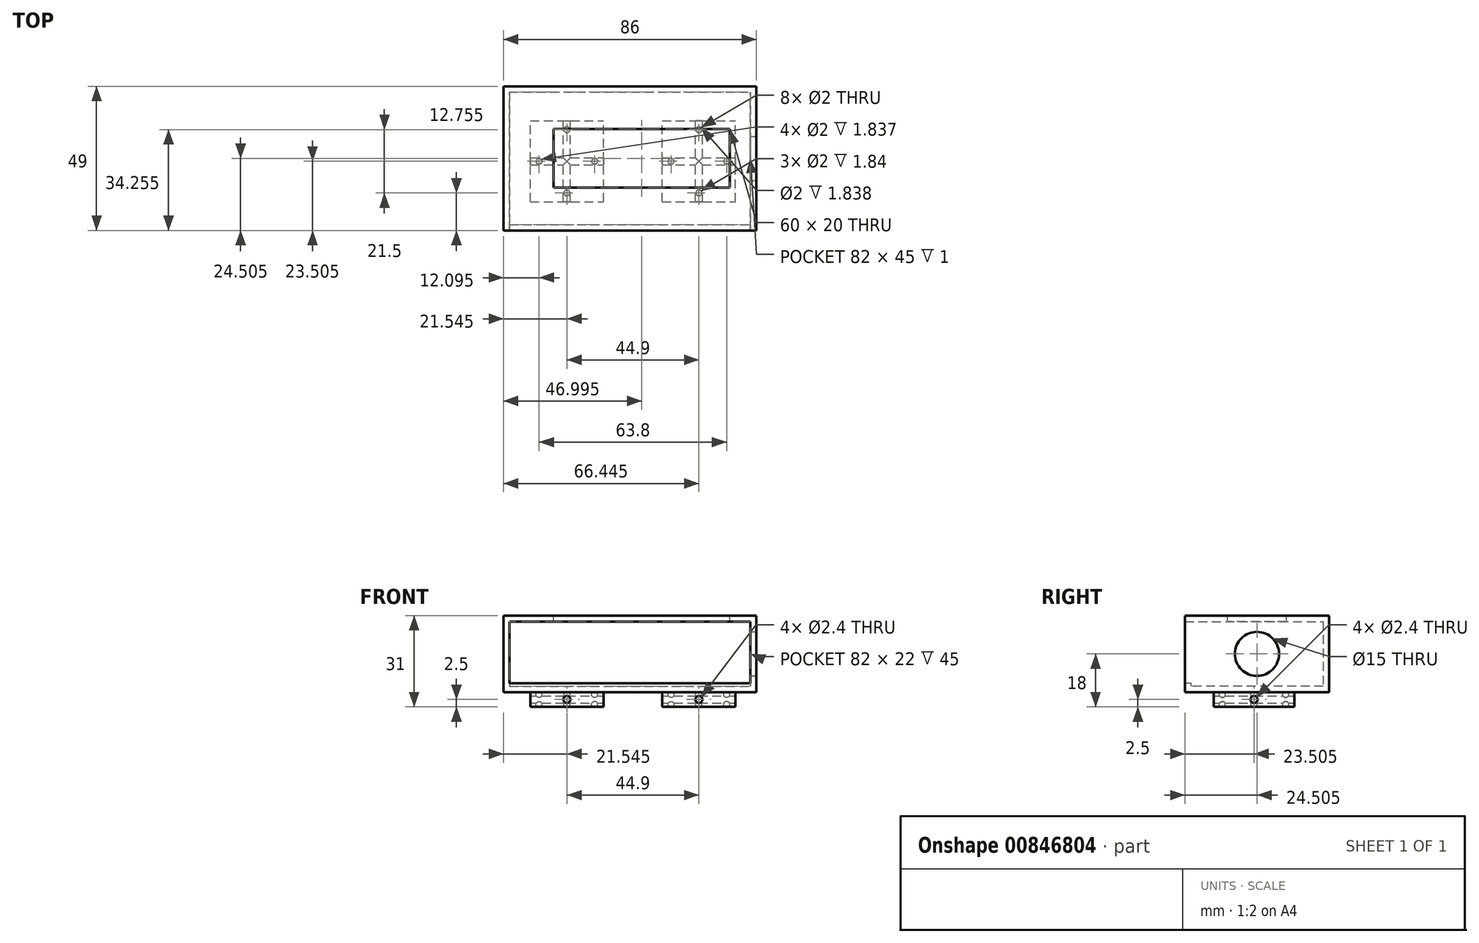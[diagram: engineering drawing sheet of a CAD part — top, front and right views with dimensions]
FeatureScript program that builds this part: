
annotation { "Feature Type Name" : "Feature", "Feature Type Description" : "" }
export const myFeature = defineFeature(function(context is Context, id is Id, definition is map)
    precondition{}
    {
        {
            var Q0;
            Q0=qCreatedBy(makeId("Top.planeOp"),FACE);
            var sketch = newSketch(context, id + "F0", { "sketchPlane" : qUnion([Q0])});
            skLineSegment(sketch, "E0.bottom", {"start": v(-27.92, 18.33) * mm, "end": v(54.08, 18.33) * mm});
            skLineSegment(sketch, "E0.top", {"start": v(-27.92, -26.67) * mm, "end": v(54.08, -26.67) * mm});
            skLineSegment(sketch, "E0.left", {"start": v(-27.92, 18.33) * mm, "end": v(-27.92, -26.67) * mm});
            skLineSegment(sketch, "E0.right", {"start": v(54.08, 18.33) * mm, "end": v(54.08, -26.67) * mm});
            skLineSegment(sketch, "E1.bottom", {"start": v(-29.92, 20.33) * mm, "end": v(56.08, 20.33) * mm});
            skLineSegment(sketch, "E1.top", {"start": v(-29.92, -28.67) * mm, "end": v(56.08, -28.67) * mm});
            skLineSegment(sketch, "E1.left", {"start": v(-29.92, 20.33) * mm, "end": v(-29.92, -28.67) * mm});
            skLineSegment(sketch, "E1.right", {"start": v(56.08, 20.33) * mm, "end": v(56.08, -28.67) * mm});
            skSolve(sketch);
        }
        {
            var Q0;
            Q0=makeQuery(id+"F0.imprint","IMPRINT",FACE,{"disambiguationData":[TD([[makeQuery(id+"F0.imprint","IMPRINT",EDGE,{"derivedFrom":sQuery(id+"F0.wireOp",EDGE,"E0.bottom")}),-1.0]])]});
            extrude(context, id + "F1", {"entities" : qUnion([Q0]), "depth" : 2 * mm, "offsetDistance" : 25 * mm});
        }
        {
            var Q0;
            Q0=makeQuery(id+"F0.imprint","IMPRINT",FACE,{"disambiguationData":[TD([[makeQuery(id+"F0.imprint","IMPRINT",EDGE,{"derivedFrom":sQuery(id+"F0.wireOp",EDGE,"E0.bottom")}),1.0]])]});
            extrude(context, id + "F2", {"entities" : qUnion([Q0]), "operationType" : NewBodyOperationType.ADD, "depth" : 26 * mm, "offsetDistance" : 25 * mm});
        }
        {
            var Q0;
            Q0=makeQuery(id+"F2.opExtrude","SWEPT_FACE",FACE,{"disambiguationData":[OSD([sQuery(id+"F0.wireOp",EDGE,"E0.bottom")])]});
            var sketch = newSketch(context, id + "F3", { "sketchPlane" : qUnion([Q0])});
            skLineSegment(sketch, "E2.bottom", {"start": v(-27.92, 26) * mm, "end": v(54.08, 26) * mm});
            skLineSegment(sketch, "E2.top", {"start": v(-27.92, 24) * mm, "end": v(54.08, 24) * mm});
            skLineSegment(sketch, "E2.left", {"start": v(-27.92, 26) * mm, "end": v(-27.92, 24) * mm});
            skLineSegment(sketch, "E2.right", {"start": v(54.08, 26) * mm, "end": v(54.08, 24) * mm});
            skSolve(sketch);
        }
        {
            var Q0;
            Q0=makeQuery(id+"F3.imprint","IMPRINT",FACE,{"disambiguationData":[TD([[makeQuery(id+"F3.imprint","IMPRINT",EDGE,{"derivedFrom":sQuery(id+"F3.wireOp",EDGE,"E2.bottom")}),-1.0]])]});
            extrude(context, id + "F4", {"entities" : qUnion([Q0]), "operationType" : NewBodyOperationType.ADD, "endBound" : BoundingType.UP_TO_NEXT, "depth" : 25 * mm, "offsetDistance" : 25 * mm});
        }
        {
            var Q0;
            Q0=makeQuery(id+"F2.opExtrude","SWEPT_FACE",FACE,{"disambiguationData":[OSD([sQuery(id+"F0.wireOp",EDGE,"E1.top")])]});
            var sketch = newSketch(context, id + "F5", { "sketchPlane" : qUnion([Q0])});
            skLineSegment(sketch, "E3.bottom", {"start": v(-27.92, 24) * mm, "end": v(54.08, 24) * mm});
            skLineSegment(sketch, "E3.top", {"start": v(-27.92, 3) * mm, "end": v(54.08, 3) * mm});
            skLineSegment(sketch, "E3.left", {"start": v(-27.92, 24) * mm, "end": v(-27.92, 3) * mm});
            skLineSegment(sketch, "E3.right", {"start": v(54.08, 24) * mm, "end": v(54.08, 3) * mm});
            skSolve(sketch);
        }
        {
            var Q0;
            Q0=makeQuery(id+"F5.imprint","IMPRINT",FACE,{"disambiguationData":[TD([[makeQuery(id+"F5.imprint","IMPRINT",EDGE,{"derivedFrom":sQuery(id+"F5.wireOp",EDGE,"E3.bottom")}),-1.0]])]});
            extrude(context, id + "F6", {"entities" : qUnion([Q0]), "operationType" : NewBodyOperationType.REMOVE, "oppositeDirection" : true, "depth" : 2 * mm, "offsetDistance" : 25 * mm});
        }
        {
            var Q0;
            Q0=makeQuery(id+"F4.boolean.opBoolean","MERGE",FACE,{"derivedFrom":[makeQuery(id+"F2.opExtrude","CAP_FACE",FACE,{"disambiguationData":[OSD([sQuery(id+"F0.wireOp",EDGE,"E0.bottom"),sQuery(id+"F0.wireOp",EDGE,"E0.top"),sQuery(id+"F0.wireOp",EDGE,"E0.left"),sQuery(id+"F0.wireOp",EDGE,"E0.right"),sQuery(id+"F0.wireOp",EDGE,"E1.bottom"),sQuery(id+"F0.wireOp",EDGE,"E1.top"),sQuery(id+"F0.wireOp",EDGE,"E1.left"),sQuery(id+"F0.wireOp",EDGE,"E1.right")])],"isStart":false}),makeQuery(id+"F4.opExtrude","SWEPT_FACE",FACE,{"disambiguationData":[OSD([sQuery(id+"F3.wireOp",EDGE,"E2.bottom")])]})]});
            var sketch = newSketch(context, id + "F7", { "sketchPlane" : qUnion([Q0])});
            skLineSegment(sketch, "E4.bottom", {"start": v(-12.92, -14.17) * mm, "end": v(47.08, -14.17) * mm});
            skLineSegment(sketch, "E4.top", {"start": v(-12.92, 5.83) * mm, "end": v(47.08, 5.83) * mm});
            skLineSegment(sketch, "E4.left", {"start": v(-12.92, -14.17) * mm, "end": v(-12.92, 5.83) * mm});
            skLineSegment(sketch, "E4.right", {"start": v(47.08, -14.17) * mm, "end": v(47.08, 5.83) * mm});
            skSolve(sketch);
        }
        {
            var Q0;
            Q0=makeQuery(id+"F7.imprint","IMPRINT",FACE,{"disambiguationData":[TD([[makeQuery(id+"F7.imprint","IMPRINT",EDGE,{"derivedFrom":sQuery(id+"F7.wireOp",EDGE,"E4.bottom")}),1.0]])]});
            extrude(context, id + "F8", {"entities" : qUnion([Q0]), "operationType" : NewBodyOperationType.REMOVE, "endBound" : BoundingType.UP_TO_NEXT, "oppositeDirection" : true, "depth" : 25 * mm, "offsetDistance" : 25 * mm});
        }
        {
            var Q0;
            Q0=makeQuery(id+"F2.opExtrude","SWEPT_FACE",FACE,{"disambiguationData":[OSD([sQuery(id+"F0.wireOp",EDGE,"E1.right")])]});
            var sketch = newSketch(context, id + "F9", { "sketchPlane" : qUnion([Q0])});
            skCircle(sketch, "E5", {"center": v(-4.17, 13) * mm, "radius": 7.5 * mm});
            skPoint(sketch, "E5.centerSnap0", {"position": v(-4.17, 26) * mm});
            skPoint(sketch, "E5.centerSnap1", {"position": v(20.33, 13) * mm});
            skSolve(sketch);
        }
        {
            var Q0;
            Q0=makeQuery(id+"F9.imprint","IMPRINT",FACE,{"disambiguationData":[TD([[makeQuery(id+"F9.imprint","IMPRINT",EDGE,{"derivedFrom":sQuery(id+"F9.wireOp",EDGE,"E5")}),1.0]])]});
            extrude(context, id + "F10", {"entities" : qUnion([Q0]), "operationType" : NewBodyOperationType.REMOVE, "endBound" : BoundingType.UP_TO_NEXT, "oppositeDirection" : true, "depth" : 25 * mm, "offsetDistance" : 25 * mm});
        }
        {
            var Q0;
            {var subQ0=sQuery(id+"F0.wireOp",EDGE,"E0.right");var subQ1=sQuery(id+"F0.wireOp",EDGE,"E0.left");var subQ2=sQuery(id+"F0.wireOp",EDGE,"E0.top");var subQ3=sQuery(id+"F0.wireOp",EDGE,"E0.bottom");Q0=makeQuery(id+"F2.boolean.opBoolean","MERGE",FACE,{"derivedFrom":[makeQuery(id+"F1.opExtrude","CAP_FACE",FACE,{"disambiguationData":[OSD([subQ3,subQ2,subQ1,subQ0])],"isStart":true}),makeQuery(id+"F2.opExtrude","CAP_FACE",FACE,{"disambiguationData":[OSD([subQ3,subQ2,subQ1,subQ0,sQuery(id+"F0.wireOp",EDGE,"E1.bottom"),sQuery(id+"F0.wireOp",EDGE,"E1.top"),sQuery(id+"F0.wireOp",EDGE,"E1.left"),sQuery(id+"F0.wireOp",EDGE,"E1.right")])],"isStart":true})]});}
            var sketch = newSketch(context, id + "F11", { "sketchPlane" : qUnion([Q0])});
            skLineSegment(sketch, "E6.bottom", {"start": v(-17.82, 15.92) * mm, "end": v(1.08, 15.92) * mm});
            skLineSegment(sketch, "E6.top", {"start": v(-17.82, -5.58) * mm, "end": v(1.08, -5.58) * mm});
            skLineSegment(sketch, "E6.left", {"start": v(-17.82, 15.92) * mm, "end": v(-17.82, -5.58) * mm});
            skLineSegment(sketch, "E6.right", {"start": v(1.08, 15.92) * mm, "end": v(1.08, -5.58) * mm});
            skLineSegment(sketch, "E7.bottom", {"start": v(-20.82, 18.92) * mm, "end": v(4.08, 18.92) * mm});
            skLineSegment(sketch, "E7.top", {"start": v(-20.82, -8.58) * mm, "end": v(4.08, -8.58) * mm});
            skLineSegment(sketch, "E7.left", {"start": v(-20.82, 18.92) * mm, "end": v(-20.82, -8.58) * mm});
            skLineSegment(sketch, "E7.right", {"start": v(4.08, 18.92) * mm, "end": v(4.08, -8.58) * mm});
            skCircle(sketch, "E8", {"center": v(1.08, 5.17) * mm, "radius": 1 * mm});
            skCircle(sketch, "E9", {"center": v(-8.37, -5.58) * mm, "radius": 1 * mm});
            skCircle(sketch, "E10", {"center": v(-17.82, 5.17) * mm, "radius": 1 * mm});
            skCircle(sketch, "E11", {"center": v(-8.37, 15.92) * mm, "radius": 1 * mm});
            skLineSegment(sketch, "E12.bottom", {"start": v(24.08, 18.92) * mm, "end": v(48.98, 18.92) * mm});
            skLineSegment(sketch, "E12.top", {"start": v(24.08, -8.58) * mm, "end": v(48.98, -8.58) * mm});
            skLineSegment(sketch, "E12.left", {"start": v(24.08, 18.92) * mm, "end": v(24.08, -8.58) * mm});
            skLineSegment(sketch, "E12.right", {"start": v(48.98, 18.92) * mm, "end": v(48.98, -8.58) * mm});
            skLineSegment(sketch, "E13.bottom", {"start": v(27.08, 15.92) * mm, "end": v(45.98, 15.92) * mm});
            skLineSegment(sketch, "E13.top", {"start": v(27.08, -5.58) * mm, "end": v(45.98, -5.58) * mm});
            skLineSegment(sketch, "E13.left", {"start": v(27.08, 15.92) * mm, "end": v(27.08, -5.58) * mm});
            skLineSegment(sketch, "E13.right", {"start": v(45.98, 15.92) * mm, "end": v(45.98, -5.58) * mm});
            skCircle(sketch, "E14", {"center": v(27.08, 5.17) * mm, "radius": 1 * mm});
            skCircle(sketch, "E15", {"center": v(36.53, 15.92) * mm, "radius": 1 * mm});
            skCircle(sketch, "E16", {"center": v(45.98, 5.17) * mm, "radius": 1 * mm});
            skCircle(sketch, "E17", {"center": v(36.53, -5.58) * mm, "radius": 1 * mm});
            skSolve(sketch);
        }
        {
            var Q0;
            Q0=makeQuery(id+"F11.imprint","IMPRINT",FACE,{"disambiguationData":[TD([[makeQuery(id+"F11.imprint","IMPRINT",EDGE,{"derivedFrom":sQuery(id+"F11.wireOp",EDGE,"E12.bottom")}),-1.0]])]});
            var Q1;
            {var subQ0=sQuery(id+"F11.wireOp",EDGE,"E14");var subQ1=sQuery(id+"F11.wireOp",EDGE,"E13.left");var subQ2=makeQuery(id+"F11.imprint","INTERSECT",VERTEX,{"disambiguationData":[OD(0.0)],"derivedFrom":[subQ1,subQ0]});Q1=makeQuery(id+"F11.imprint","IMPRINT",FACE,{"disambiguationData":[TD([[makeQuery(id+"F11.imprint","IMPRINT",EDGE,{"disambiguationData":[TD([[subQ2,-1.0]])],"derivedFrom":subQ1}),-1.0]])]});}
            var Q2;
            {var subQ0=sQuery(id+"F11.wireOp",EDGE,"E14");var subQ1=sQuery(id+"F11.wireOp",EDGE,"E13.left");var subQ2=makeQuery(id+"F11.imprint","INTERSECT",VERTEX,{"disambiguationData":[OD(0.0)],"derivedFrom":[subQ1,subQ0]});Q2=makeQuery(id+"F11.imprint","IMPRINT",FACE,{"disambiguationData":[TD([[makeQuery(id+"F11.imprint","IMPRINT",EDGE,{"disambiguationData":[TD([[subQ2,-1.0]])],"derivedFrom":subQ1}),1.0]])]});}
            var Q3;
            {var subQ0=sQuery(id+"F11.wireOp",EDGE,"E15");var subQ1=sQuery(id+"F11.wireOp",EDGE,"E13.bottom");var subQ2=makeQuery(id+"F11.imprint","INTERSECT",VERTEX,{"disambiguationData":[OD(0.0)],"derivedFrom":[subQ1,subQ0]});Q3=makeQuery(id+"F11.imprint","IMPRINT",FACE,{"disambiguationData":[TD([[makeQuery(id+"F11.imprint","IMPRINT",EDGE,{"disambiguationData":[TD([[subQ2,-1.0]])],"derivedFrom":subQ1}),-1.0]])]});}
            var Q4;
            {var subQ0=sQuery(id+"F11.wireOp",EDGE,"E15");var subQ1=sQuery(id+"F11.wireOp",EDGE,"E13.bottom");var subQ2=makeQuery(id+"F11.imprint","INTERSECT",VERTEX,{"disambiguationData":[OD(0.0)],"derivedFrom":[subQ1,subQ0]});Q4=makeQuery(id+"F11.imprint","IMPRINT",FACE,{"disambiguationData":[TD([[makeQuery(id+"F11.imprint","IMPRINT",EDGE,{"disambiguationData":[TD([[subQ2,-1.0]])],"derivedFrom":subQ1}),1.0]])]});}
            var Q5;
            {var subQ0=sQuery(id+"F11.wireOp",EDGE,"E16");var subQ1=sQuery(id+"F11.wireOp",EDGE,"E13.right");var subQ2=makeQuery(id+"F11.imprint","INTERSECT",VERTEX,{"disambiguationData":[OD(0.0)],"derivedFrom":[subQ1,subQ0]});Q5=makeQuery(id+"F11.imprint","IMPRINT",FACE,{"disambiguationData":[TD([[makeQuery(id+"F11.imprint","IMPRINT",EDGE,{"disambiguationData":[TD([[subQ2,-1.0]])],"derivedFrom":subQ1}),-1.0]])]});}
            var Q6;
            {var subQ0=sQuery(id+"F11.wireOp",EDGE,"E16");var subQ1=sQuery(id+"F11.wireOp",EDGE,"E13.right");var subQ2=makeQuery(id+"F11.imprint","INTERSECT",VERTEX,{"disambiguationData":[OD(0.0)],"derivedFrom":[subQ1,subQ0]});Q6=makeQuery(id+"F11.imprint","IMPRINT",FACE,{"disambiguationData":[TD([[makeQuery(id+"F11.imprint","IMPRINT",EDGE,{"disambiguationData":[TD([[subQ2,-1.0]])],"derivedFrom":subQ1}),1.0]])]});}
            var Q7;
            {var subQ0=sQuery(id+"F11.wireOp",EDGE,"E17");var subQ1=sQuery(id+"F11.wireOp",EDGE,"E13.top");var subQ2=makeQuery(id+"F11.imprint","INTERSECT",VERTEX,{"disambiguationData":[OD(0.0)],"derivedFrom":[subQ1,subQ0]});Q7=makeQuery(id+"F11.imprint","IMPRINT",FACE,{"disambiguationData":[TD([[makeQuery(id+"F11.imprint","IMPRINT",EDGE,{"disambiguationData":[TD([[subQ2,-1.0]])],"derivedFrom":subQ1}),-1.0]])]});}
            var Q8;
            Q8=makeQuery(id+"F11.imprint","IMPRINT",FACE,{"disambiguationData":[TD([[makeQuery(id+"F11.imprint","IMPRINT",EDGE,{"derivedFrom":sQuery(id+"F11.wireOp",EDGE,"E7.bottom")}),-1.0]])]});
            var Q9;
            {var subQ0=sQuery(id+"F11.wireOp",EDGE,"E9");var subQ1=sQuery(id+"F11.wireOp",EDGE,"E6.top");var subQ2=makeQuery(id+"F11.imprint","INTERSECT",VERTEX,{"disambiguationData":[OD(0.0)],"derivedFrom":[subQ1,subQ0]});Q9=makeQuery(id+"F11.imprint","IMPRINT",FACE,{"disambiguationData":[TD([[makeQuery(id+"F11.imprint","IMPRINT",EDGE,{"disambiguationData":[TD([[subQ2,-1.0]])],"derivedFrom":subQ1}),-1.0]])]});}
            var Q10;
            {var subQ0=sQuery(id+"F11.wireOp",EDGE,"E9");var subQ1=sQuery(id+"F11.wireOp",EDGE,"E6.top");var subQ2=makeQuery(id+"F11.imprint","INTERSECT",VERTEX,{"disambiguationData":[OD(0.0)],"derivedFrom":[subQ1,subQ0]});Q10=makeQuery(id+"F11.imprint","IMPRINT",FACE,{"disambiguationData":[TD([[makeQuery(id+"F11.imprint","IMPRINT",EDGE,{"disambiguationData":[TD([[subQ2,-1.0]])],"derivedFrom":subQ1}),1.0]])]});}
            var Q11;
            {var subQ0=sQuery(id+"F11.wireOp",EDGE,"E8");var subQ1=sQuery(id+"F11.wireOp",EDGE,"E6.right");var subQ2=makeQuery(id+"F11.imprint","INTERSECT",VERTEX,{"disambiguationData":[OD(0.0)],"derivedFrom":[subQ1,subQ0]});Q11=makeQuery(id+"F11.imprint","IMPRINT",FACE,{"disambiguationData":[TD([[makeQuery(id+"F11.imprint","IMPRINT",EDGE,{"disambiguationData":[TD([[subQ2,-1.0]])],"derivedFrom":subQ1}),-1.0]])]});}
            var Q12;
            {var subQ0=sQuery(id+"F11.wireOp",EDGE,"E8");var subQ1=sQuery(id+"F11.wireOp",EDGE,"E6.right");var subQ2=makeQuery(id+"F11.imprint","INTERSECT",VERTEX,{"disambiguationData":[OD(0.0)],"derivedFrom":[subQ1,subQ0]});Q12=makeQuery(id+"F11.imprint","IMPRINT",FACE,{"disambiguationData":[TD([[makeQuery(id+"F11.imprint","IMPRINT",EDGE,{"disambiguationData":[TD([[subQ2,-1.0]])],"derivedFrom":subQ1}),1.0]])]});}
            var Q13;
            {var subQ0=sQuery(id+"F11.wireOp",EDGE,"E11");var subQ1=sQuery(id+"F11.wireOp",EDGE,"E6.bottom");var subQ2=makeQuery(id+"F11.imprint","INTERSECT",VERTEX,{"disambiguationData":[OD(0.0)],"derivedFrom":[subQ1,subQ0]});Q13=makeQuery(id+"F11.imprint","IMPRINT",FACE,{"disambiguationData":[TD([[makeQuery(id+"F11.imprint","IMPRINT",EDGE,{"disambiguationData":[TD([[subQ2,-1.0]])],"derivedFrom":subQ1}),1.0]])]});}
            var Q14;
            {var subQ0=sQuery(id+"F11.wireOp",EDGE,"E11");var subQ1=sQuery(id+"F11.wireOp",EDGE,"E6.bottom");var subQ2=makeQuery(id+"F11.imprint","INTERSECT",VERTEX,{"disambiguationData":[OD(0.0)],"derivedFrom":[subQ1,subQ0]});Q14=makeQuery(id+"F11.imprint","IMPRINT",FACE,{"disambiguationData":[TD([[makeQuery(id+"F11.imprint","IMPRINT",EDGE,{"disambiguationData":[TD([[subQ2,-1.0]])],"derivedFrom":subQ1}),-1.0]])]});}
            var Q15;
            {var subQ0=sQuery(id+"F11.wireOp",EDGE,"E10");var subQ1=sQuery(id+"F11.wireOp",EDGE,"E6.left");var subQ2=makeQuery(id+"F11.imprint","INTERSECT",VERTEX,{"disambiguationData":[OD(0.0)],"derivedFrom":[subQ1,subQ0]});Q15=makeQuery(id+"F11.imprint","IMPRINT",FACE,{"disambiguationData":[TD([[makeQuery(id+"F11.imprint","IMPRINT",EDGE,{"disambiguationData":[TD([[subQ2,-1.0]])],"derivedFrom":subQ1}),1.0]])]});}
            var Q16;
            {var subQ0=sQuery(id+"F11.wireOp",EDGE,"E10");var subQ1=sQuery(id+"F11.wireOp",EDGE,"E6.left");var subQ2=makeQuery(id+"F11.imprint","INTERSECT",VERTEX,{"disambiguationData":[OD(0.0)],"derivedFrom":[subQ1,subQ0]});Q16=makeQuery(id+"F11.imprint","IMPRINT",FACE,{"disambiguationData":[TD([[makeQuery(id+"F11.imprint","IMPRINT",EDGE,{"disambiguationData":[TD([[subQ2,-1.0]])],"derivedFrom":subQ1}),-1.0]])]});}
            var Q17;
            {var subQ0=sQuery(id+"F11.wireOp",EDGE,"E17");var subQ1=sQuery(id+"F11.wireOp",EDGE,"E13.top");var subQ2=makeQuery(id+"F11.imprint","INTERSECT",VERTEX,{"disambiguationData":[OD(0.0)],"derivedFrom":[subQ1,subQ0]});Q17=makeQuery(id+"F11.imprint","IMPRINT",FACE,{"disambiguationData":[TD([[makeQuery(id+"F11.imprint","IMPRINT",EDGE,{"disambiguationData":[TD([[subQ2,-1.0]])],"derivedFrom":subQ1}),1.0]])]});}
            extrude(context, id + "F12", {"entities" : qUnion([Q0, Q1, Q2, Q3, Q4, Q5, Q6, Q7, Q8, Q9, Q10, Q11, Q12, Q13, Q14, Q15, Q16, Q17]), "operationType" : NewBodyOperationType.ADD, "depth" : 5 * mm, "offsetDistance" : 25 * mm});
        }
        {
            var Q0;
            Q0=makeQuery(id+"F12.opExtrude","SWEPT_FACE",FACE,{"disambiguationData":[OSD([sQuery(id+"F11.wireOp",EDGE,"E12.right")])]});
            var sketch = newSketch(context, id + "F13", { "sketchPlane" : qUnion([Q0])});
            skPoint(sketch, "E18", {"position": v(-5.17, -2.5) * mm});
            skPoint(sketch, "E18.positionSnap0", {"position": v(-18.92, -2.5) * mm});
            skPoint(sketch, "E18.positionSnap1", {"position": v(-5.17, -5) * mm});
            skSolve(sketch);
        }
        {
            var Q0;
            Q0=sQuery(id+"F13.wireOp",VERTEX,"E18");
            var Q1;
            Q1=makeQuery(id+"F1.opExtrude","SWEPT_BODY",BODY,{"disambiguationData":[OSD([sQuery(id+"F0.wireOp",EDGE,"E0.bottom"),sQuery(id+"F0.wireOp",EDGE,"E0.top"),sQuery(id+"F0.wireOp",EDGE,"E0.left"),sQuery(id+"F0.wireOp",EDGE,"E0.right")])]});
            hole(context, id + "F14", {"style" : HoleStyle.SIMPLE, "endStyle" : HoleEndStyle.THROUGH, "holeDiameter" : 2.4 * mm, "majorDiameter" : 5 * mm, "isTappedThrough" : true, "tappedDepth" : 12 * mm, "tapClearance" : 3, "locations" : qUnion([Q0]), "scope" : qUnion([Q1])});
        }
        {
            var Q0;
            Q0=makeQuery(id+"F12.opExtrude","SWEPT_FACE",FACE,{"disambiguationData":[OSD([sQuery(id+"F11.wireOp",EDGE,"E12.top")])]});
            var sketch = newSketch(context, id + "F15", { "sketchPlane" : qUnion([Q0])});
            skPoint(sketch, "E19", {"position": v(-36.53, -2.5) * mm});
            skPoint(sketch, "E19.positionSnap0", {"position": v(-36.53, -5) * mm});
            skPoint(sketch, "E19.positionSnap1", {"position": v(-48.98, -2.5) * mm});
            skSolve(sketch);
        }
        {
            var Q0;
            Q0=sQuery(id+"F15.wireOp",VERTEX,"E19");
            var Q1;
            Q1=makeQuery(id+"F1.opExtrude","SWEPT_BODY",BODY,{"disambiguationData":[OSD([sQuery(id+"F0.wireOp",EDGE,"E0.bottom"),sQuery(id+"F0.wireOp",EDGE,"E0.top"),sQuery(id+"F0.wireOp",EDGE,"E0.left"),sQuery(id+"F0.wireOp",EDGE,"E0.right")])]});
            hole(context, id + "F16", {"style" : HoleStyle.SIMPLE, "endStyle" : HoleEndStyle.THROUGH, "holeDiameter" : 2.4 * mm, "majorDiameter" : 5 * mm, "isTappedThrough" : true, "tappedDepth" : 12 * mm, "tapClearance" : 3, "locations" : qUnion([Q0]), "scope" : qUnion([Q1])});
        }
        {
            var Q0;
            Q0=makeQuery(id+"F12.opExtrude","SWEPT_FACE",FACE,{"disambiguationData":[OSD([sQuery(id+"F11.wireOp",EDGE,"E7.top")])]});
            var sketch = newSketch(context, id + "F17", { "sketchPlane" : qUnion([Q0])});
            skPoint(sketch, "E20", {"position": v(8.37, -2.5) * mm});
            skPoint(sketch, "E20.positionSnap0", {"position": v(8.37, -5) * mm});
            skPoint(sketch, "E20.positionSnap1", {"position": v(-4.08, -2.5) * mm});
            skSolve(sketch);
        }
        {
            var Q0;
            Q0=sQuery(id+"F17.wireOp",VERTEX,"E20");
            var Q1;
            Q1=makeQuery(id+"F1.opExtrude","SWEPT_BODY",BODY,{"disambiguationData":[OSD([sQuery(id+"F0.wireOp",EDGE,"E0.bottom"),sQuery(id+"F0.wireOp",EDGE,"E0.top"),sQuery(id+"F0.wireOp",EDGE,"E0.left"),sQuery(id+"F0.wireOp",EDGE,"E0.right")])]});
            hole(context, id + "F18", {"style" : HoleStyle.SIMPLE, "endStyle" : HoleEndStyle.THROUGH, "holeDiameter" : 2.4 * mm, "majorDiameter" : 5 * mm, "isTappedThrough" : true, "tappedDepth" : 12 * mm, "tapClearance" : 3, "locations" : qUnion([Q0]), "scope" : qUnion([Q1])});
        }
    });
